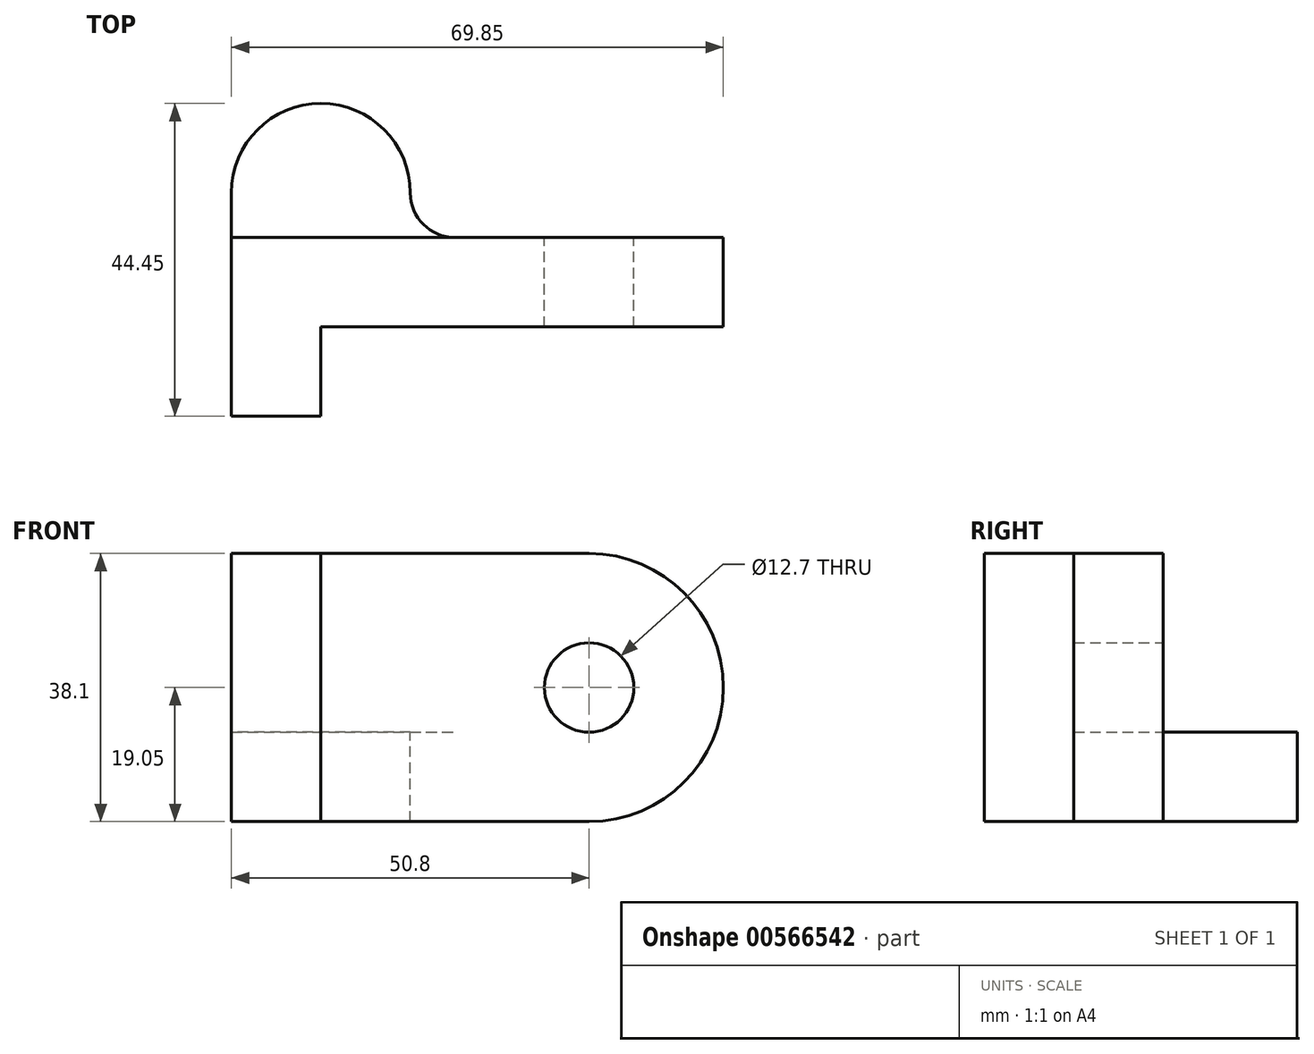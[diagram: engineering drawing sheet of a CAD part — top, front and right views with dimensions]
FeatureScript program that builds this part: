
annotation { "Feature Type Name" : "Feature", "Feature Type Description" : "" }
export const myFeature = defineFeature(function(context is Context, id is Id, definition is map)
    precondition{}
    {
        {
            var Q0;
            Q0=qCreatedBy(makeId("Front.planeOp"),FACE);
            var sketch = newSketch(context, id + "F0", { "sketchPlane" : qUnion([Q0])});
            skLineSegment(sketch, "E0.bottom", {"start": v(0, 0) * mm, "end": v(-50.8, 0) * mm});
            skLineSegment(sketch, "E0.top", {"start": v(0, -19.05) * mm, "end": v(-50.8, -19.05) * mm});
            skLineSegment(sketch, "E0.left", {"start": v(0, 0) * mm, "end": v(0, -19.05) * mm});
            skLineSegment(sketch, "E0.right", {"start": v(-50.8, 0) * mm, "end": v(-50.8, -19.05) * mm});
            skLineSegment(sketch, "E1.top", {"start": v(0, 19.05) * mm, "end": v(-50.8, 19.05) * mm});
            skLineSegment(sketch, "E1.left", {"start": v(0, 0) * mm, "end": v(0, 19.05) * mm});
            skLineSegment(sketch, "E1.right", {"start": v(-50.8, 0) * mm, "end": v(-50.8, 19.05) * mm});
            skCircle(sketch, "E2", {"center": v(0, 0) * mm, "radius": 19.05 * mm});
            skLineSegment(sketch, "E3", {"start": v(-19.05, 0) * mm, "end": v(19.05, 0) * mm});
            skLineSegment(sketch, "E4", {"start": v(19.05, 0) * mm, "end": v(0, 0) * mm});
            skCircle(sketch, "E5", {"center": v(0, 0) * mm, "radius": 6.35 * mm});
            skSolve(sketch);
        }
        {
            var Q0;
            Q0 = qSketchRegion(id + "F0", true);
            extrude(context, id + "F1", {"entities" : qUnion([Q0]), "depth" : 12.7 * mm, "offsetDistance" : 25.4 * mm});
        }
        {
            var Q0;
            Q0=makeQuery(id+"F1.opExtrude","CAP_FACE",FACE,{"disambiguationData":[OSD([sQuery(id+"F0.wireOp",EDGE,"E0.top"),sQuery(id+"F0.wireOp",EDGE,"E0.right"),sQuery(id+"F0.wireOp",EDGE,"E1.top"),sQuery(id+"F0.wireOp",EDGE,"E1.right"),sQuery(id+"F0.wireOp",EDGE,"E2"),sQuery(id+"F0.wireOp",EDGE,"E5")])],"isStart":false});
            var sketch = newSketch(context, id + "F2", { "sketchPlane" : qUnion([Q0])});
            skLineSegment(sketch, "E6", {"start": v(0, 0) * mm, "end": v(-50.8, 0) * mm});
            skLineSegment(sketch, "E7", {"start": v(-50.8, 0) * mm, "end": v(-50.8, 19.05) * mm});
            skLineSegment(sketch, "E8", {"start": v(-50.8, 19.05) * mm, "end": v(-50.8, -19.05) * mm});
            skLineSegment(sketch, "E9", {"start": v(-50.8, -19.05) * mm, "end": v(-38.1, -19.05) * mm});
            skLineSegment(sketch, "E10", {"start": v(-38.1, -19.05) * mm, "end": v(-38.1, 0) * mm});
            skLineSegment(sketch, "E11", {"start": v(-38.1, 0) * mm, "end": v(-38.1, 19.05) * mm});
            skLineSegment(sketch, "E12", {"start": v(-38.1, 19.05) * mm, "end": v(-50.8, 19.05) * mm});
            skSolve(sketch);
        }
        {
            var Q0;
            Q0 = qSketchRegion(id + "F2", true);
            extrude(context, id + "F3", {"entities" : qUnion([Q0]), "operationType" : NewBodyOperationType.ADD, "depth" : 12.7 * mm, "offsetDistance" : 25.4 * mm});
        }
        {
            var Q0;
            Q0=makeQuery(id+"F1.opExtrude","CAP_FACE",FACE,{"disambiguationData":[OSD([sQuery(id+"F0.wireOp",EDGE,"E0.top"),sQuery(id+"F0.wireOp",EDGE,"E0.right"),sQuery(id+"F0.wireOp",EDGE,"E1.top"),sQuery(id+"F0.wireOp",EDGE,"E1.right"),sQuery(id+"F0.wireOp",EDGE,"E2"),sQuery(id+"F0.wireOp",EDGE,"E5")])],"isStart":true});
            var sketch = newSketch(context, id + "F4", { "sketchPlane" : qUnion([Q0])});
            skLineSegment(sketch, "E13.bottom", {"start": v(50.8, -19.05) * mm, "end": v(19.05, -19.05) * mm});
            skLineSegment(sketch, "E13.left", {"start": v(50.8, -19.05) * mm, "end": v(50.8, -6.35) * mm});
            skLineSegment(sketch, "E14.top", {"start": v(50.8, -6.35) * mm, "end": v(19.05, -6.35) * mm});
            skLineSegment(sketch, "E14.right", {"start": v(19.05, -19.05) * mm, "end": v(19.05, -6.35) * mm});
            skSolve(sketch);
        }
        {
            var Q0;
            Q0 = qSketchRegion(id + "F4", true);
            extrude(context, id + "F5", {"entities" : qUnion([Q0]), "operationType" : NewBodyOperationType.ADD, "depth" : 6.35 * mm, "offsetDistance" : 25.4 * mm});
        }
        {
            var Q0;
            Q0=makeQuery(id+"F5.opExtrude","SWEPT_FACE",FACE,{"disambiguationData":[OSD([sQuery(id+"F4.wireOp",EDGE,"E14.top")])]});
            var sketch = newSketch(context, id + "F6", { "sketchPlane" : qUnion([Q0])});
            skCircle(sketch, "E15", {"center": v(-19.05, 6.35) * mm, "radius": 6.35 * mm});
            skSolve(sketch);
        }
        {
            var Q0;
            Q0 = qSketchRegion(id + "F6", true);
            extrude(context, id + "F7", {"entities" : qUnion([Q0]), "operationType" : NewBodyOperationType.REMOVE, "oppositeDirection" : true, "depth" : 25.4 * mm, "offsetDistance" : 25.4 * mm});
        }
        {
            var Q0;
            Q0=makeQuery(id+"F5.opExtrude","SWEPT_FACE",FACE,{"disambiguationData":[OSD([sQuery(id+"F4.wireOp",EDGE,"E14.top")])]});
            var sketch = newSketch(context, id + "F8", { "sketchPlane" : qUnion([Q0])});
            skLineSegment(sketch, "E16.bottom", {"start": v(-50.8, 0) * mm, "end": v(-25.4, 0) * mm});
            skLineSegment(sketch, "E16.top", {"start": v(-50.8, 6.35) * mm, "end": v(-25.4, 6.35) * mm});
            skLineSegment(sketch, "E16.left", {"start": v(-50.8, 0) * mm, "end": v(-50.8, 6.35) * mm});
            skLineSegment(sketch, "E16.right", {"start": v(-25.4, 0) * mm, "end": v(-25.4, 6.35) * mm});
            skLineSegment(sketch, "E17", {"start": v(-50.8, 6.35) * mm, "end": v(-38.1, 6.35) * mm});
            skArc(sketch, "E18", {"start": v(-25.4, 6.35) * mm, "mid": v(-38.1, 19.05) * mm, "end": v(-50.8, 6.35) * mm});
            skLineSegment(sketch, "E19", {"start": v(-38.1, 6.35) * mm, "end": v(-38.1, 0) * mm});
            skLineSegment(sketch, "E20", {"start": v(-38.1, 0) * mm, "end": v(-50.8, 0) * mm});
            skSolve(sketch);
        }
        {
            var Q0;
            Q0=makeQuery(id+"F8.imprint","IMPRINT",FACE,{"disambiguationData":[TD([[makeQuery(id+"F8.imprint","IMPRINT",EDGE,{"derivedFrom":sQuery(id+"F8.wireOp",EDGE,"E16.top")}),1.0]])]});
            extrude(context, id + "F9", {"entities" : qUnion([Q0]), "operationType" : NewBodyOperationType.ADD, "oppositeDirection" : true, "depth" : 12.7 * mm, "offsetDistance" : 25.4 * mm});
        }
    });
